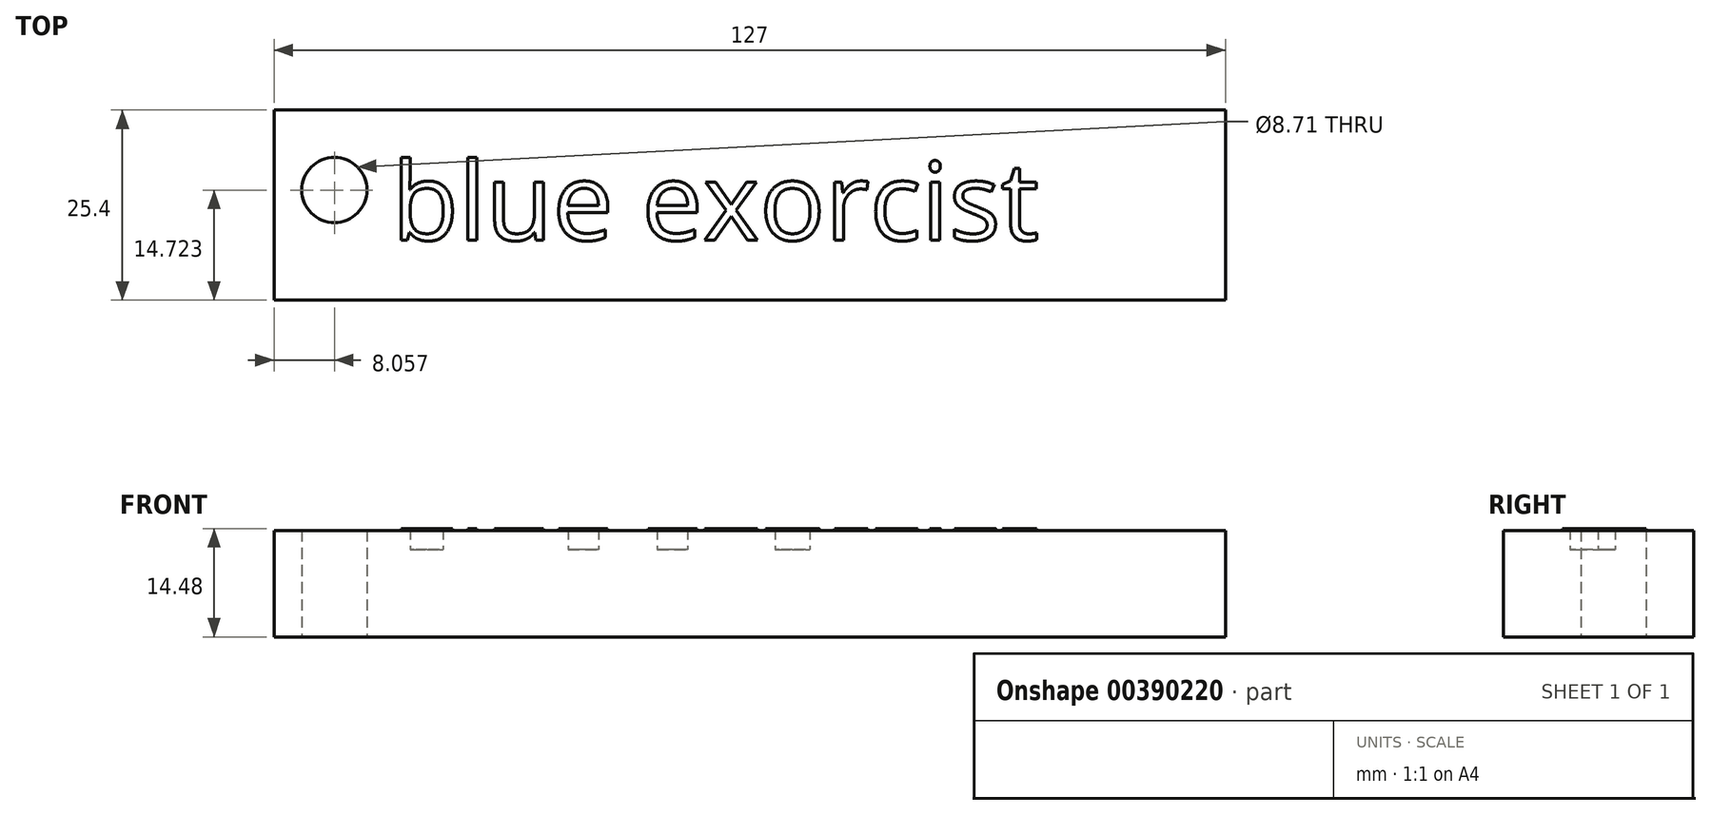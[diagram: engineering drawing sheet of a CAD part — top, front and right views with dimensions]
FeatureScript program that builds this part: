
annotation { "Feature Type Name" : "Feature", "Feature Type Description" : "" }
export const myFeature = defineFeature(function(context is Context, id is Id, definition is map)
    precondition{}
    {
        {
            var Q0;
            Q0=qCreatedBy(makeId("Top.planeOp"),FACE);
            var sketch = newSketch(context, id + "F0", { "sketchPlane" : qUnion([Q0])});
            skLineSegment(sketch, "E0.bottom", {"start": v(-33.5, 45.6) * mm, "end": v(93.5, 45.6) * mm});
            skLineSegment(sketch, "E0.top", {"start": v(-33.5, 20.2) * mm, "end": v(93.5, 20.2) * mm});
            skLineSegment(sketch, "E0.left", {"start": v(-33.5, 45.6) * mm, "end": v(-33.5, 20.2) * mm});
            skLineSegment(sketch, "E0.right", {"start": v(93.5, 45.6) * mm, "end": v(93.5, 20.2) * mm});
            skSolve(sketch);
        }
        {
            var Q0;
            Q0=makeQuery(id+"F0.imprint","IMPRINT",FACE,{"disambiguationData":[TD([[makeQuery(id+"F0.imprint","IMPRINT",EDGE,{"derivedFrom":sQuery(id+"F0.wireOp",EDGE,"E0.bottom")}),-1.0]])]});
            var sketch = newSketch(context, id + "F1", { "sketchPlane" : qUnion([Q0])});
            skCircle(sketch, "E1", {"center": v(-25.45, 34.92) * mm, "radius": 4.36 * mm});
            skSolve(sketch);
        }
        {
            var Q0;
            Q0=makeQuery(id+"F1.imprint","IMPRINT",FACE,{"disambiguationData":[TD([[makeQuery(id+"F1.imprint","IMPRINT",EDGE,{"derivedFrom":sQuery(id+"F1.wireOp",EDGE,"E1")}),-1.0]])]});
            extrude(context, id + "F2", {"entities" : qUnion([Q0]), "depth" : 11.68 * mm});
        }
        {
            var Q0;
            Q0=makeQuery(id+"F2.opExtrude","CAP_FACE",FACE,{"disambiguationData":[OSD([sQuery(id+"F0.wireOp",EDGE,"E0.bottom"),sQuery(id+"F0.wireOp",EDGE,"E0.top"),sQuery(id+"F0.wireOp",EDGE,"E0.left"),sQuery(id+"F0.wireOp",EDGE,"E0.right"),sQuery(id+"F1.wireOp",EDGE,"E1")])],"isStart":false});
            var sketch = newSketch(context, id + "F3", { "sketchPlane" : qUnion([Q0])});
            skText(sketch, "E2", { "text": "blue exorcist ", "fontName": "OpenSans-Regular.ttf"});
            const initialGuessF3  = {"E2": [-0.01778, 0.02823, 1, 0, 0.01044]};
            skSetInitialGuess(sketch, initialGuessF3);
            skSolve(sketch);
        }
        {
            var Q0;
            Q0 = qSketchRegion(id + "F3", true);
            var Q1;
            Q1=makeQuery(id+"F3.imprint","IMPRINT",FACE,{"disambiguationData":[TD([[makeQuery(id+"F3.imprint","IMPRINT",EDGE,{"derivedFrom":sQuery(id+"F3.wireOp",EDGE,"E2.sketch_text.stroke-0")}),1.0]])]});
            extrude(context, id + "F4", {"entities" : qUnion([Q0, Q1]), "operationType" : NewBodyOperationType.ADD, "depth" : 2.54 * mm});
        }
        {
            var Q0;
            Q0 = qSketchRegion(id + "F3", true);
            extrude(context, id + "F5", {"entities" : qUnion([Q0]), "operationType" : NewBodyOperationType.ADD, "depth" : 2.8 * mm});
        }
    });
